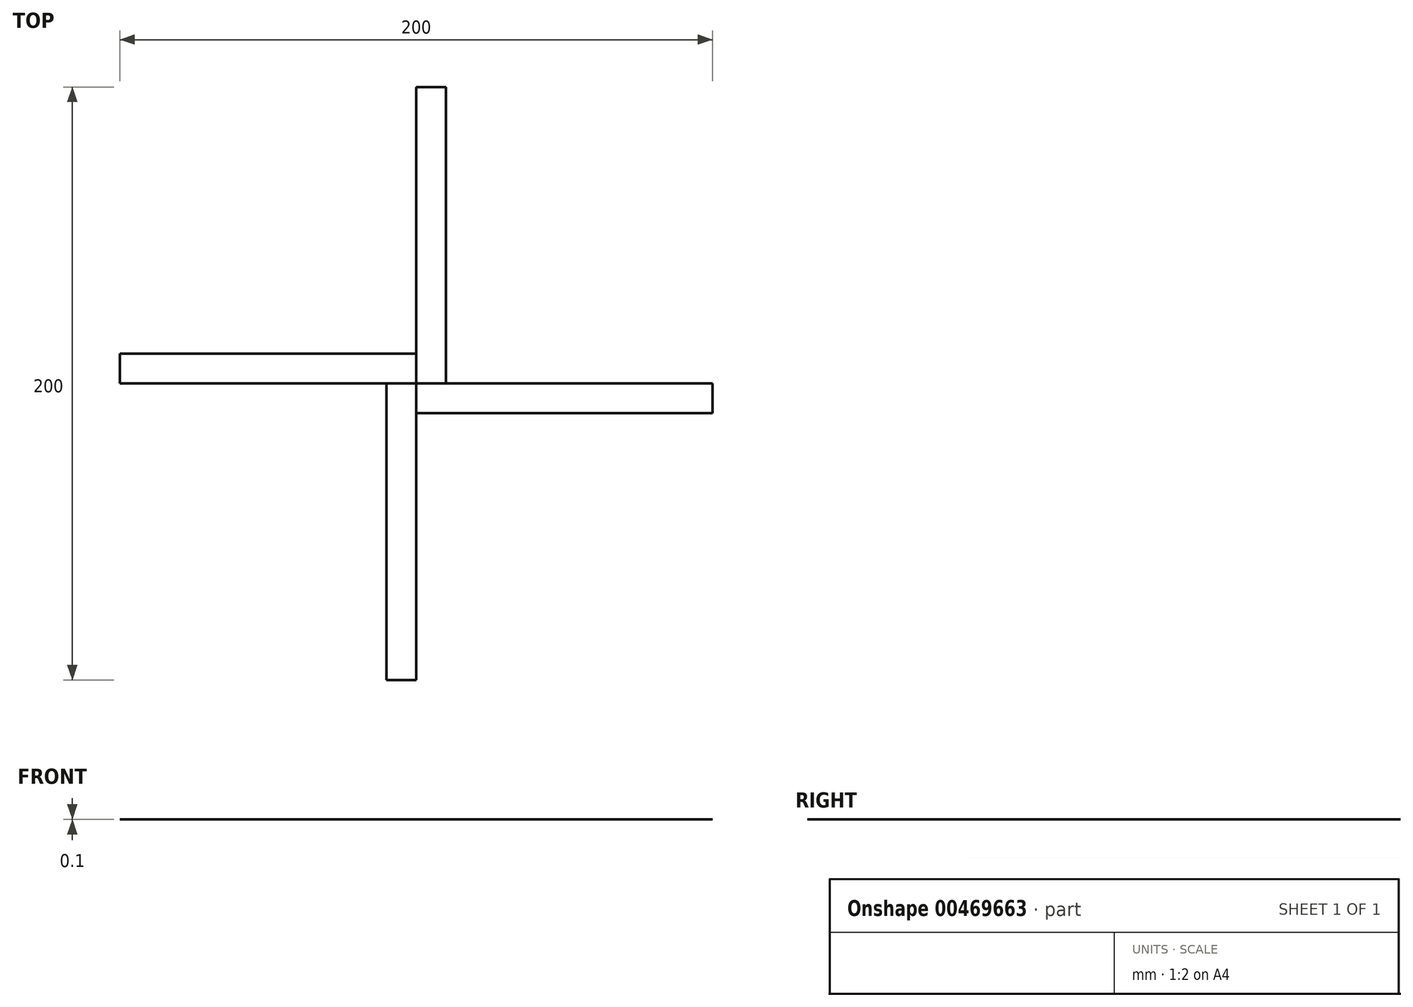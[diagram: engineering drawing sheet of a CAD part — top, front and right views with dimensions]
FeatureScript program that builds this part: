
annotation { "Feature Type Name" : "Feature", "Feature Type Description" : "" }
export const myFeature = defineFeature(function(context is Context, id is Id, definition is map)
    precondition{}
    {
        {
            assignVariable(context, id + "F0", {"name" : "paleL", "anyValue" : 100});
        }
        {
            var Q0;
            Q0=qCreatedBy(makeId("Front.planeOp"),FACE);
            var sketch = newSketch(context, id + "F1", { "sketchPlane" : qUnion([Q0])});
            skLineSegment(sketch, "E0.bottom", {"start": v(-102.27, 29.16) * mm, "end": v(-92.27, 29.16) * mm});
            skLineSegment(sketch, "E0.top", {"start": v(-102.27, 29.06) * mm, "end": v(-92.27, 29.06) * mm});
            skLineSegment(sketch, "E0.left", {"start": v(-102.27, 29.16) * mm, "end": v(-102.27, 29.06) * mm});
            skLineSegment(sketch, "E0.right", {"start": v(-92.27, 29.16) * mm, "end": v(-92.27, 29.06) * mm});
            skSolve(sketch);
        }
        {
            var Q0;
            Q0=makeQuery(id+"F1.imprint","IMPRINT",FACE,{"disambiguationData":[TD([[makeQuery(id+"F1.imprint","IMPRINT",EDGE,{"derivedFrom":sQuery(id+"F1.wireOp",EDGE,"E0.bottom")}),-1.0]])]});
            extrude(context, id + "F2", {"entities" : qUnion([Q0]), "oppositeDirection" : true, "depth" : (getVariable(context, 'paleL')) * mm});
        }
        {
            var Q0;
            Q0=makeQuery(id+"F2.opExtrude","SWEPT_BODY",BODY,{"disambiguationData":[OSD([sQuery(id+"F1.wireOp",EDGE,"E0.bottom"),sQuery(id+"F1.wireOp",EDGE,"E0.top"),sQuery(id+"F1.wireOp",EDGE,"E0.left"),sQuery(id+"F1.wireOp",EDGE,"E0.right")])]});
            var Q1;
            Q1=makeQuery(id+"F2.opExtrude","CAP_EDGE",EDGE,{"disambiguationData":[OSD([sQuery(id+"F1.wireOp",EDGE,"E0.left")])],"isStart":true});
            circularPattern(context, id + "F3", {"entities" : qUnion([Q0]), "axis" : qUnion([Q1]), "angle" : 360 * degree, "instanceCount" : 4, "equalSpace" : true});
        }
    });
